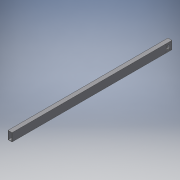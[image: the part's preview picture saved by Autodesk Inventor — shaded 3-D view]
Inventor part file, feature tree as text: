
AUTODESK INVENTOR PART (.ipt)
format: ipt  version: 2018 (Build 220112000, 112)  size: 135,680 bytes
history: native  units: in
note: dims shown in document units (in); Inventor stores cm internally (conversion verified against a paired STEP export)
features: extrude x3, sketch x3
ambient origin geometry x8: Origin, YZ Plane, XZ Plane, XY Plane, X Axis, Y Axis, Z Axis, Center Point
bodies: Solid1 (feature_tree)
feature tree (6):
  extrude  "Extrusion1"  Depth=2.0in
  extrude  "Extrusion2"  Depth=39.7in TaperAngle=0.0deg
  extrude  "Extrusion3"  Depth=1.0in TaperAngle=0.0deg
  sketch  "Sketch1"  dims[d0=1.0in d1=2.0in]
  sketch  "Sketch2"  dims[d2=0.125in d3=39.7in d4=0.0in]
  sketch  "Sketch3"  dims[d5=1.0in d7=10.0in d8=0.0in d9=1.0in d10=0.188in d11=0.531in d12=0.938in d13=1.624in d14=1.624in d15=0.2031in d16=0.2031in d17=0.2031in d18=0.2031in d19=1.0in d20=0.0in]
